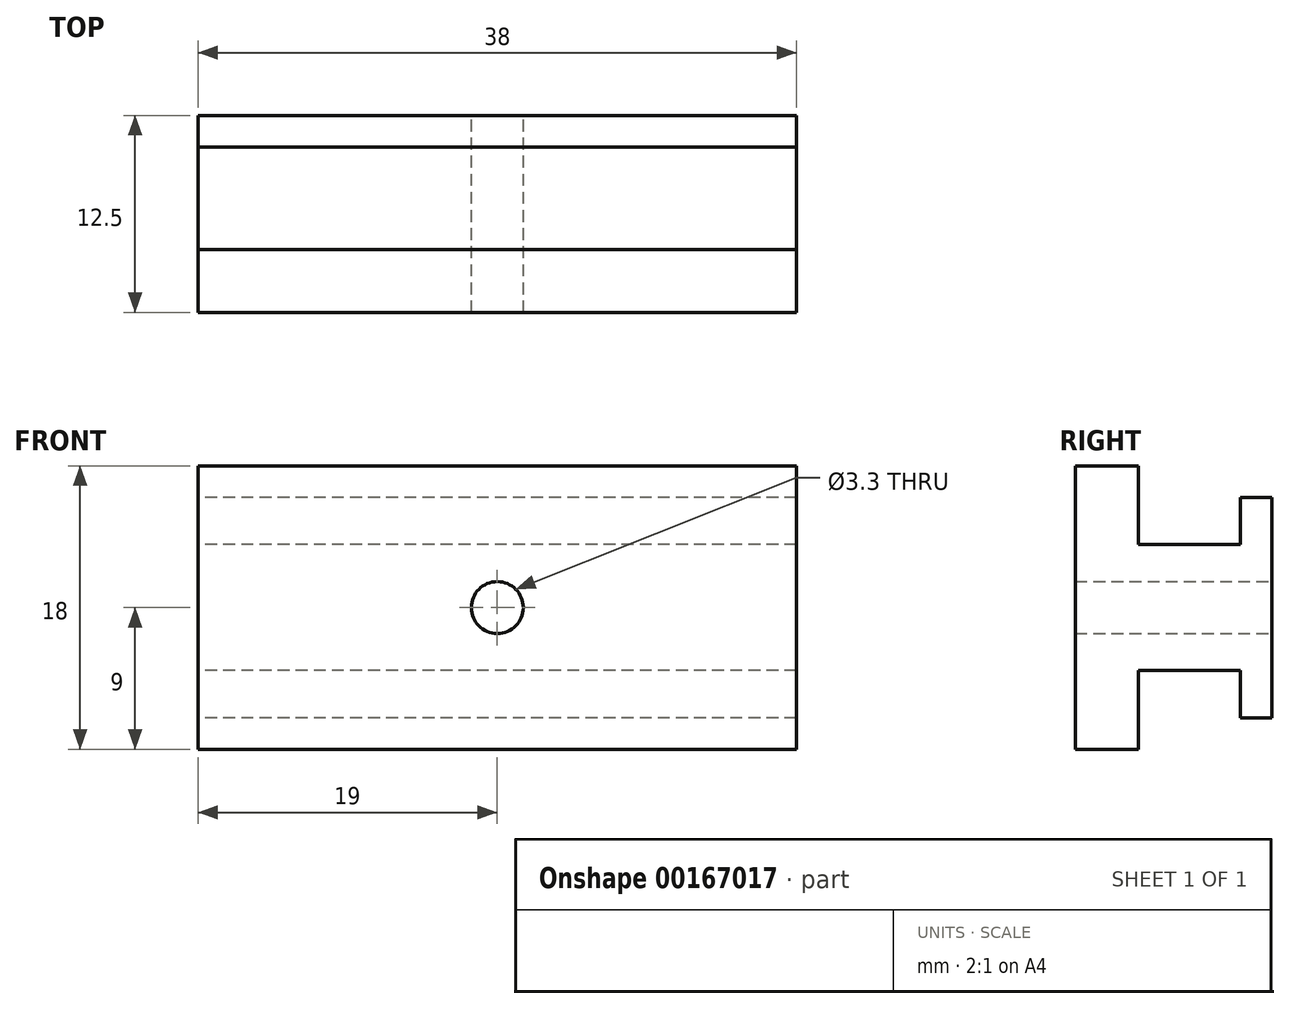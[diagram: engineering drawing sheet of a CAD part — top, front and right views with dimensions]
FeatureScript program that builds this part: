
annotation { "Feature Type Name" : "Feature", "Feature Type Description" : "" }
export const myFeature = defineFeature(function(context is Context, id is Id, definition is map)
    precondition{}
    {
        {
            var Q0;
            Q0=qCreatedBy(makeId("Right.planeOp"),FACE);
            var sketch = newSketch(context, id + "F0", { "sketchPlane" : qUnion([Q0])});
            skLineSegment(sketch, "E0", {"start": v(0, 15) * mm, "end": v(6.1, 15) * mm});
            skLineSegment(sketch, "E1", {"start": v(20, 20) * mm, "end": v(15, 20) * mm});
            skLineSegment(sketch, "E2.0", {"start": v(15, 20) * mm, "end": v(15, 24) * mm});
            skLineSegment(sketch, "E3.0", {"start": v(11, 24) * mm, "end": v(11, 15) * mm});
            skLineSegment(sketch, "E4.trimOffspring", {"start": v(15, 24) * mm, "end": v(11, 24) * mm});
            skLineSegment(sketch, "E5", {"start": v(15, 20) * mm, "end": v(15, 19) * mm});
            skLineSegment(sketch, "E6", {"start": v(15, 19) * mm, "end": v(21.5, 19) * mm});
            skLineSegment(sketch, "E7", {"start": v(21.5, 19) * mm, "end": v(21.5, 22) * mm});
            skLineSegment(sketch, "E8", {"start": v(21.5, 22) * mm, "end": v(23.5, 22) * mm});
            skLineSegment(sketch, "E9", {"start": v(23.5, 22) * mm, "end": v(23.5, 15) * mm});
            skLineSegment(sketch, "E10.MirrorCS", {"start": v(15, 10) * mm, "end": v(15, 11) * mm});
            skLineSegment(sketch, "E11.MirrorCS", {"start": v(20, 10) * mm, "end": v(15, 10) * mm});
            skLineSegment(sketch, "E12.MirrorCS", {"start": v(21.5, 8) * mm, "end": v(23.5, 8) * mm});
            skLineSegment(sketch, "E13.MirrorCS", {"start": v(23.5, 8) * mm, "end": v(23.5, 15) * mm});
            skLineSegment(sketch, "E14.MirrorCS", {"start": v(21.5, 11) * mm, "end": v(21.5, 8) * mm});
            skLineSegment(sketch, "E15.MirrorCS", {"start": v(15, 11) * mm, "end": v(21.5, 11) * mm});
            skLineSegment(sketch, "E16.MirrorCS", {"start": v(15, 6) * mm, "end": v(11, 6) * mm});
            skLineSegment(sketch, "E17.MirrorCS", {"start": v(11, 6) * mm, "end": v(11, 15) * mm});
            skLineSegment(sketch, "E18.MirrorCS", {"start": v(15, 10) * mm, "end": v(15, 6) * mm});
            skSolve(sketch);
        }
        {
            var Q0;
            Q0 = qSketchRegion(id + "F0", true);
            extrude(context, id + "F1", {"entities" : qUnion([Q0]), "depth" : 38 * mm});
        }
        {
            var Q0;
            Q0=makeQuery(id+"F1.opExtrude","SWEPT_FACE",FACE,{"disambiguationData":[OSD([sQuery(id+"F0.wireOp",EDGE,"E9"),sQuery(id+"F0.wireOp",EDGE,"3e864bbd-24f3-4d39-9146-677a4ecd5e8a0.MirrorCS")])]});
            var sketch = newSketch(context, id + "F2", { "sketchPlane" : qUnion([Q0])});
            skLineSegment(sketch, "E19", {"start": v(-19, 22) * mm, "end": v(-19, 8) * mm});
            skCircle(sketch, "E20", {"center": v(-19, 15) * mm, "radius": 1.65 * mm});
            skSolve(sketch);
        }
        {
            var Q0;
            Q0 = qSketchRegion(id + "F2", true);
            extrude(context, id + "F3", {"entities" : qUnion([Q0]), "operationType" : NewBodyOperationType.REMOVE, "oppositeDirection" : true, "depth" : 25 * mm});
        }
    });
